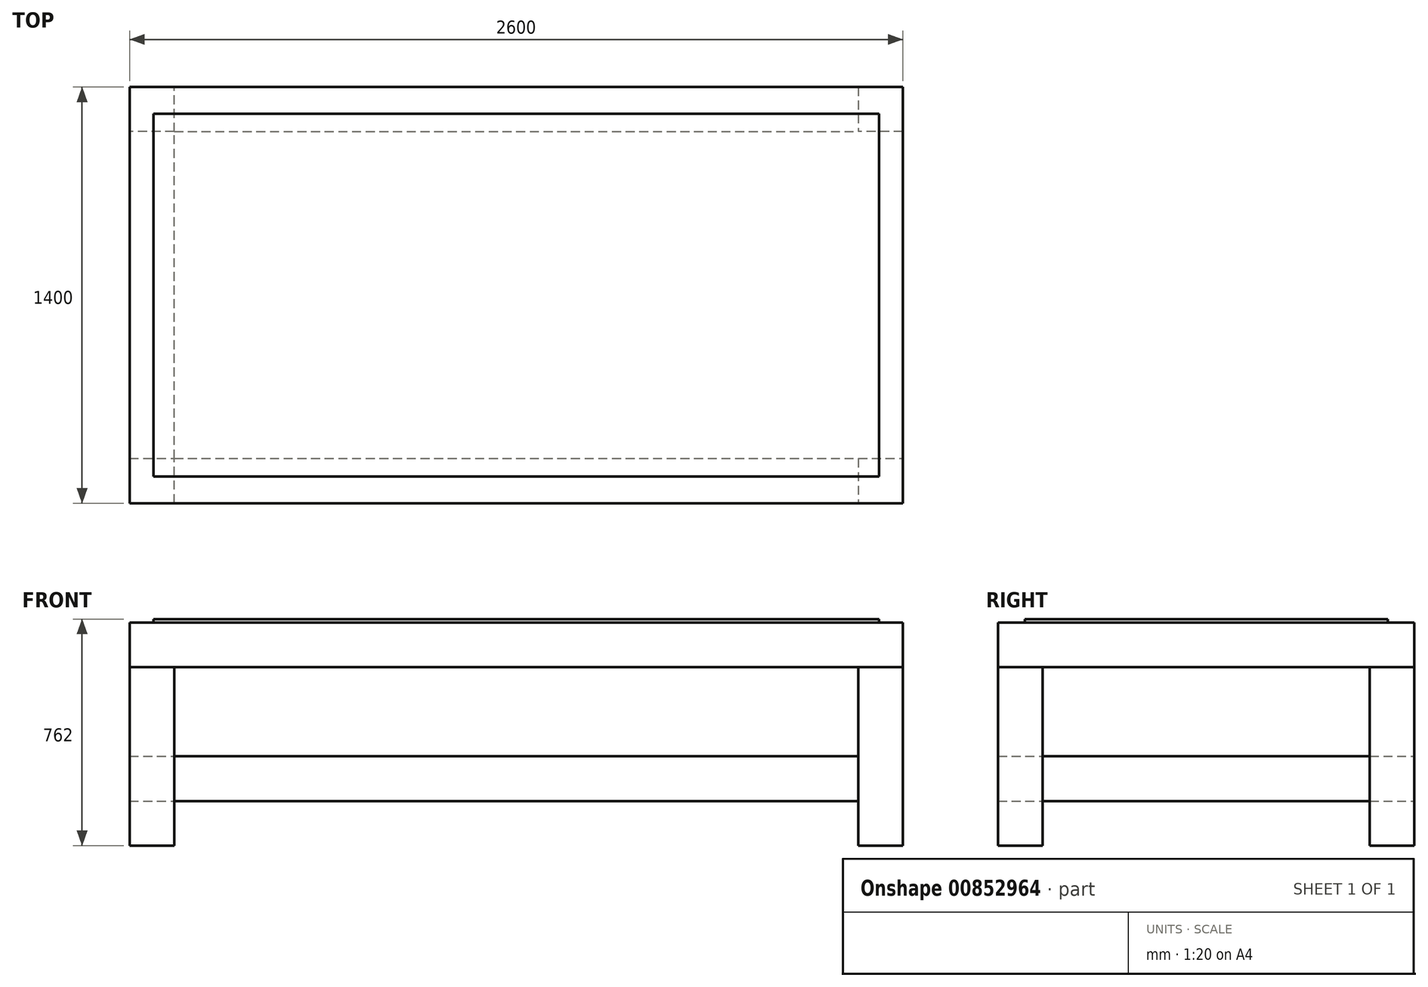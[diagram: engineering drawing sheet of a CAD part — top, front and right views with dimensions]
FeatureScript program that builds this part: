
annotation { "Feature Type Name" : "Feature", "Feature Type Description" : "" }
export const myFeature = defineFeature(function(context is Context, id is Id, definition is map)
    precondition{}
    {
        {
            var Q0;
            Q0=qCreatedBy(makeId("Top.planeOp"),FACE);
            var sketch = newSketch(context, id + "F0", { "sketchPlane" : qUnion([Q0])});
            skLineSegment(sketch, "E0.bottom", {"start": v(1220, 610) * mm, "end": v(-1220, 610) * mm});
            skLineSegment(sketch, "E0.top", {"start": v(1220, -610) * mm, "end": v(-1220, -610) * mm});
            skLineSegment(sketch, "E0.left", {"start": v(1220, 610) * mm, "end": v(1220, -610) * mm});
            skLineSegment(sketch, "E0.right", {"start": v(-1220, 610) * mm, "end": v(-1220, -610) * mm});
            skPoint(sketch, "E0.middle", {"position": v(0, 0) * mm});
            skSolve(sketch);
        }
        {
            var Q0;
            Q0=makeQuery(id+"F0.imprint","IMPRINT",FACE,{"disambiguationData":[TD([[makeQuery(id+"F0.imprint","IMPRINT",EDGE,{"derivedFrom":sQuery(id+"F0.wireOp",EDGE,"E0.bottom")}),1.0]])]});
            extrude(context, id + "F1", {"entities" : qUnion([Q0]), "depth" : 12 * mm, "offsetDistance" : 25 * mm});
        }
        {
            var Q0;
            Q0=qCreatedBy(makeId("Top.planeOp"),FACE);
            var sketch = newSketch(context, id + "F2", { "sketchPlane" : qUnion([Q0])});
            skLineSegment(sketch, "E1.bottom", {"start": v(1300, -700) * mm, "end": v(-1300, -700) * mm});
            skLineSegment(sketch, "E1.top", {"start": v(1300, 700) * mm, "end": v(-1300, 700) * mm});
            skLineSegment(sketch, "E1.left", {"start": v(1300, -700) * mm, "end": v(1300, 700) * mm});
            skLineSegment(sketch, "E1.right", {"start": v(-1300, -700) * mm, "end": v(-1300, 700) * mm});
            skPoint(sketch, "E1.middle", {"position": v(0, 0) * mm});
            skSolve(sketch);
        }
        {
            var Q0;
            Q0=makeQuery(id+"F2.imprint","IMPRINT",FACE,{"disambiguationData":[TD([[makeQuery(id+"F2.imprint","IMPRINT",EDGE,{"derivedFrom":sQuery(id+"F2.wireOp",EDGE,"E1.bottom")}),-1.0]])]});
            extrude(context, id + "F3", {"entities" : qUnion([Q0]), "oppositeDirection" : true, "depth" : 150 * mm, "offsetDistance" : 25 * mm});
        }
        {
            var Q0;
            Q0=makeQuery(id+"F3.opExtrude","CAP_FACE",FACE,{"disambiguationData":[OSD([sQuery(id+"F2.wireOp",EDGE,"E1.bottom"),sQuery(id+"F2.wireOp",EDGE,"E1.top"),sQuery(id+"F2.wireOp",EDGE,"E1.left"),sQuery(id+"F2.wireOp",EDGE,"E1.right")])],"isStart":false});
            var sketch = newSketch(context, id + "F4", { "sketchPlane" : qUnion([Q0])});
            skLineSegment(sketch, "E2.bottom", {"start": v(-1300, 700) * mm, "end": v(-1150, 700) * mm});
            skLineSegment(sketch, "E2.top", {"start": v(-1300, 550) * mm, "end": v(-1150, 550) * mm});
            skLineSegment(sketch, "E2.left", {"start": v(-1300, 700) * mm, "end": v(-1300, 550) * mm});
            skLineSegment(sketch, "E2.right", {"start": v(-1150, 700) * mm, "end": v(-1150, 550) * mm});
            skSolve(sketch);
        }
        {
            var Q0;
            Q0=makeQuery(id+"F4.imprint","IMPRINT",FACE,{"disambiguationData":[TD([[makeQuery(id+"F4.imprint","IMPRINT",EDGE,{"derivedFrom":sQuery(id+"F4.wireOp",EDGE,"E2.bottom")}),1.0]])]});
            extrude(context, id + "F5", {"entities" : qUnion([Q0]), "depth" : 600 * mm, "offsetDistance" : 25 * mm});
        }
        {
            var Q0;
            Q0=makeQuery(id+"F5.opExtrude","SWEPT_BODY",BODY,{"disambiguationData":[OSD([sQuery(id+"F4.wireOp",EDGE,"E2.bottom"),sQuery(id+"F4.wireOp",EDGE,"E2.top"),sQuery(id+"F4.wireOp",EDGE,"E2.left"),sQuery(id+"F4.wireOp",EDGE,"E2.right")])]});
            transform(context, id + "F6", {"entities" : qUnion([Q0]), "transformType" : TransformType.TRANSLATION_3D, "dx" : 2450 * mm, "dy" : 0 * mm, "dz" : 0 * mm, "makeCopy" : true});
        }
        {
            var Q0;
            Q0=makeQuery(id+"F5.opExtrude","SWEPT_BODY",BODY,{"disambiguationData":[OSD([sQuery(id+"F4.wireOp",EDGE,"E2.bottom"),sQuery(id+"F4.wireOp",EDGE,"E2.top"),sQuery(id+"F4.wireOp",EDGE,"E2.left"),sQuery(id+"F4.wireOp",EDGE,"E2.right")])]});
            transform(context, id + "F7", {"entities" : qUnion([Q0]), "transformType" : TransformType.TRANSLATION_3D, "dx" : 0 * mm, "dy" : 1250 * mm, "dz" : 0 * mm, "makeCopy" : true});
        }
        {
            var Q0;
            Q0=makeQuery(id+"F6.opPattern","COPY",BODY,{"derivedFrom":makeQuery(id+"F5.opExtrude","SWEPT_BODY",BODY,{"disambiguationData":[OSD([sQuery(id+"F4.wireOp",EDGE,"E2.bottom"),sQuery(id+"F4.wireOp",EDGE,"E2.top"),sQuery(id+"F4.wireOp",EDGE,"E2.left"),sQuery(id+"F4.wireOp",EDGE,"E2.right")])]}),"instanceName":"1"});
            transform(context, id + "F8", {"entities" : qUnion([Q0]), "transformType" : TransformType.TRANSLATION_3D, "dx" : 0 * mm, "dy" : 1250 * mm, "dz" : 0 * mm, "makeCopy" : true});
        }
        {
            var Q0;
            Q0=makeQuery(id+"F8.opPattern","COPY",FACE,{"derivedFrom":makeQuery(id+"F6.opPattern","COPY",FACE,{"derivedFrom":makeQuery(id+"F5.opExtrude","SWEPT_FACE",FACE,{"disambiguationData":[OSD([sQuery(id+"F4.wireOp",EDGE,"E2.left")])]}),"instanceName":"1"}),"instanceName":"1"});
            var sketch = newSketch(context, id + "F9", { "sketchPlane" : qUnion([Q0])});
            skLineSegment(sketch, "E3.bottom", {"start": v(-700, -600) * mm, "end": v(-550, -600) * mm});
            skLineSegment(sketch, "E3.top", {"start": v(-700, -450) * mm, "end": v(-550, -450) * mm});
            skLineSegment(sketch, "E3.left", {"start": v(-700, -600) * mm, "end": v(-700, -450) * mm});
            skLineSegment(sketch, "E3.right", {"start": v(-550, -600) * mm, "end": v(-550, -450) * mm});
            skSolve(sketch);
        }
        {
            var Q0;
            Q0=makeQuery(id+"F9.imprint","IMPRINT",FACE,{"disambiguationData":[TD([[makeQuery(id+"F9.imprint","IMPRINT",EDGE,{"derivedFrom":sQuery(id+"F9.wireOp",EDGE,"E3.bottom")}),1.0]])]});
            extrude(context, id + "F10", {"entities" : qUnion([Q0]), "endBound" : BoundingType.UP_TO_NEXT, "depth" : 89 * mm, "offsetDistance" : 25 * mm});
        }
        {
            var Q0;
            Q0=makeQuery(id+"F10.opExtrude","SWEPT_BODY",BODY,{"disambiguationData":[OSD([sQuery(id+"F9.wireOp",EDGE,"E3.bottom"),sQuery(id+"F9.wireOp",EDGE,"E3.top"),sQuery(id+"F9.wireOp",EDGE,"E3.left"),sQuery(id+"F9.wireOp",EDGE,"E3.right")])]});
            transform(context, id + "F11", {"entities" : qUnion([Q0]), "transformType" : TransformType.TRANSLATION_3D, "dx" : 0 * mm, "dy" : -1250 * mm, "dz" : 0 * mm, "makeCopy" : true});
        }
        {
            var Q0;
            Q0=qCreatedBy(makeId("Front.planeOp"),FACE);
            var sketch = newSketch(context, id + "F12", { "sketchPlane" : qUnion([Q0])});
            skLineSegment(sketch, "E4.bottom", {"start": v(-1300, -600) * mm, "end": v(-1150, -600) * mm});
            skLineSegment(sketch, "E4.top", {"start": v(-1300, -450) * mm, "end": v(-1150, -450) * mm});
            skLineSegment(sketch, "E4.left", {"start": v(-1300, -600) * mm, "end": v(-1300, -450) * mm});
            skLineSegment(sketch, "E4.right", {"start": v(-1150, -600) * mm, "end": v(-1150, -450) * mm});
            skSolve(sketch);
        }
        {
            var Q0;
            Q0=makeQuery(id+"F12.imprint","IMPRINT",FACE,{"disambiguationData":[TD([[makeQuery(id+"F12.imprint","IMPRINT",EDGE,{"derivedFrom":sQuery(id+"F12.wireOp",EDGE,"E4.bottom")}),1.0]])]});
            var Q1;
            Q1=makeQuery(id+"F7.opPattern","COPY",FACE,{"derivedFrom":makeQuery(id+"F5.opExtrude","SWEPT_FACE",FACE,{"disambiguationData":[OSD([sQuery(id+"F4.wireOp",EDGE,"E2.bottom")])]}),"instanceName":"1"});
            extrude(context, id + "F13", {"entities" : qUnion([Q0]), "endBound" : BoundingType.UP_TO_NEXT, "depth" : 1250 * mm, "offsetDistance" : 25 * mm, "hasSecondDirection" : true, "secondDirectionBound" : SecondDirectionBoundingType.UP_TO_SURFACE, "secondDirectionOppositeDirection" : true, "secondDirectionDepth" : 370 * mm, "secondDirectionBoundEntityFace" : qUnion([Q1])});
        }
    });
